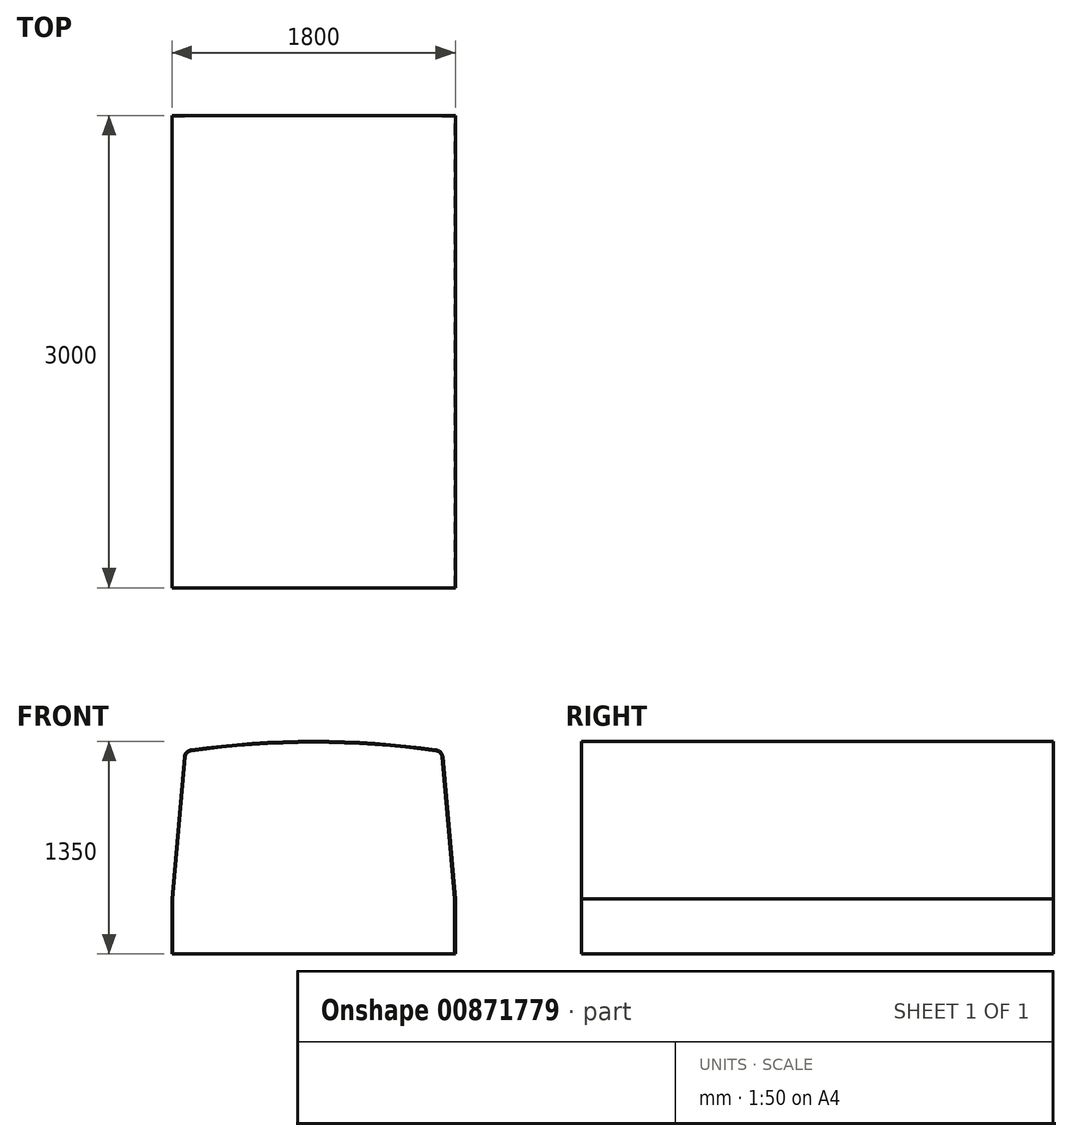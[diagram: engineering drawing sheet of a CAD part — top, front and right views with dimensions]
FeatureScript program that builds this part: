
annotation { "Feature Type Name" : "Feature", "Feature Type Description" : "" }
export const myFeature = defineFeature(function(context is Context, id is Id, definition is map)
    precondition{}
    {
        {
            var Q0;
            Q0=qCreatedBy(makeId("Front.planeOp"),FACE);
            var sketch = newSketch(context, id + "F0", { "sketchPlane" : qUnion([Q0])});
            skLineSegment(sketch, "E0", {"start": v(-900, 0) * mm, "end": v(-821.22, 900.44) * mm});
            skLineSegment(sketch, "E1", {"start": v(-771.41, 946.08) * mm, "end": v(-737.93, 946.08) * mm, "construction": true});
            skLineSegment(sketch, "E2", {"start": v(821.22, 900.44) * mm, "end": v(900, 0) * mm});
            skLineSegment(sketch, "E3", {"start": v(900, 0) * mm, "end": v(894.98, 0) * mm});
            skPoint(sketch, "E4.visualSharp", {"position": v(-817.23, 946.08) * mm});
            skArc(sketch, "E4.filletArc", {"start": v(-778.37, 945.6) * mm, "mid": v(-807.68, 930.5) * mm, "end": v(-821.22, 900.44) * mm});
            skPoint(sketch, "E5.visualSharp", {"position": v(817.23, 946.08) * mm});
            skArc(sketch, "E5.filletArc", {"start": v(821.22, 900.44) * mm, "mid": v(807.68, 930.5) * mm, "end": v(778.37, 945.6) * mm});
            skLineSegment(sketch, "E6.0", {"start": v(816.24, 900) * mm, "end": v(894.98, 0) * mm});
            skArc(sketch, "E7", {"start": v(-777.67, 940.64) * mm, "mid": v(-804.05, 927.05) * mm, "end": v(-816.24, 900) * mm});
            skLineSegment(sketch, "E8.trimOffspring", {"start": v(-894.98, 0) * mm, "end": v(-816.24, 900) * mm});
            skArc(sketch, "E9", {"start": v(816.24, 900) * mm, "mid": v(804.05, 927.05) * mm, "end": v(777.67, 940.64) * mm});
            skLineSegment(sketch, "E10.trimOffspring", {"start": v(-894.98, 0) * mm, "end": v(-900, 0) * mm});
            skLineSegment(sketch, "E11", {"start": v(-816.24, 900) * mm, "end": v(816.24, 900) * mm, "construction": true});
            skLineSegment(sketch, "E12", {"start": v(894.98, 0) * mm, "end": v(-894.98, 0) * mm, "construction": true});
            skPoint(sketch, "E13", {"position": v(0, 900) * mm});
            skPoint(sketch, "E14", {"position": v(0, 1000) * mm});
            skArc(sketch, "E15", {"start": v(778.37, 945.6) * mm, "mid": v(0, 1000) * mm, "end": v(-778.37, 945.6) * mm});
            skArc(sketch, "E16.0", {"start": v(777.67, 940.64) * mm, "mid": v(0, 995) * mm, "end": v(-777.67, 940.64) * mm});
            skLineSegment(sketch, "E17.trimOffspring", {"start": v(737.93, 946.08) * mm, "end": v(771.41, 946.08) * mm, "construction": true});
            skSolve(sketch);
        }
        {
            var Q0;
            Q0=makeQuery(id+"F0.imprint","IMPRINT",FACE,{"disambiguationData":[TD([[makeQuery(id+"F0.imprint","IMPRINT",EDGE,{"derivedFrom":sQuery(id+"F0.wireOp",EDGE,"E0")}),-1.0]])]});
            extrude(context, id + "F1", {"entities" : qUnion([Q0]), "depth" : 3000 * mm, "offsetDistance" : 25 * mm});
        }
        {
            var Q0;
            Q0=makeQuery(id+"F1.opExtrude","CAP_FACE",FACE,{"disambiguationData":[OSD([sQuery(id+"F0.wireOp",EDGE,"E0"),sQuery(id+"F0.wireOp",EDGE,"E1"),sQuery(id+"F0.wireOp",EDGE,"E2"),sQuery(id+"F0.wireOp",EDGE,"E3"),sQuery(id+"F0.wireOp",EDGE,"E4.filletArc"),sQuery(id+"F0.wireOp",EDGE,"E5.filletArc"),sQuery(id+"F0.wireOp",EDGE,"cff533d0-b0d8-4237-93ef-065a5c2e9636.0"),sQuery(id+"F0.wireOp",EDGE,"E6.0"),sQuery(id+"F0.wireOp",EDGE,"E7"),sQuery(id+"F0.wireOp",EDGE,"E8.trimOffspring"),sQuery(id+"F0.wireOp",EDGE,"E9"),sQuery(id+"F0.wireOp",EDGE,"E10.trimOffspring")])],"isStart":true});
            var sketch = newSketch(context, id + "F2", { "sketchPlane" : qUnion([Q0])});
            skLineSegment(sketch, "E18", {"start": v(-894.98, 0) * mm, "end": v(894.98, 0) * mm});
            skSolve(sketch);
        }
        {
            var Q0;
            Q0=makeQuery(id+"F2.imprint","IMPRINT",FACE,{"disambiguationData":[TD([[makeQuery(id+"F2.imprint","IMPRINT",EDGE,{"derivedFrom":sQuery(id+"F2.wireOp",EDGE,"E18")}),1.0]])]});
            extrude(context, id + "F3", {"entities" : qUnion([Q0]), "operationType" : NewBodyOperationType.ADD, "oppositeDirection" : true, "depth" : 5 * mm, "offsetDistance" : 25 * mm});
        }
        {
            var Q0;
            Q0=makeQuery(id+"F3.boolean.opBoolean","MERGE",FACE,{"derivedFrom":[makeQuery(id+"F1.opExtrude","SWEPT_FACE",FACE,{"disambiguationData":[OSD([sQuery(id+"F0.wireOp",EDGE,"E3")])]}),makeQuery(id+"F1.opExtrude","SWEPT_FACE",FACE,{"disambiguationData":[OSD([sQuery(id+"F0.wireOp",EDGE,"E10.trimOffspring")])]}),makeQuery(id+"F3.opExtrude","SWEPT_FACE",FACE,{"disambiguationData":[OSD([sQuery(id+"F2.wireOp",EDGE,"E18")])]})]});
            extrude(context, id + "F4", {"entities" : qUnion([Q0]), "operationType" : NewBodyOperationType.ADD, "depth" : 350 * mm, "offsetDistance" : 25 * mm});
        }
    });
